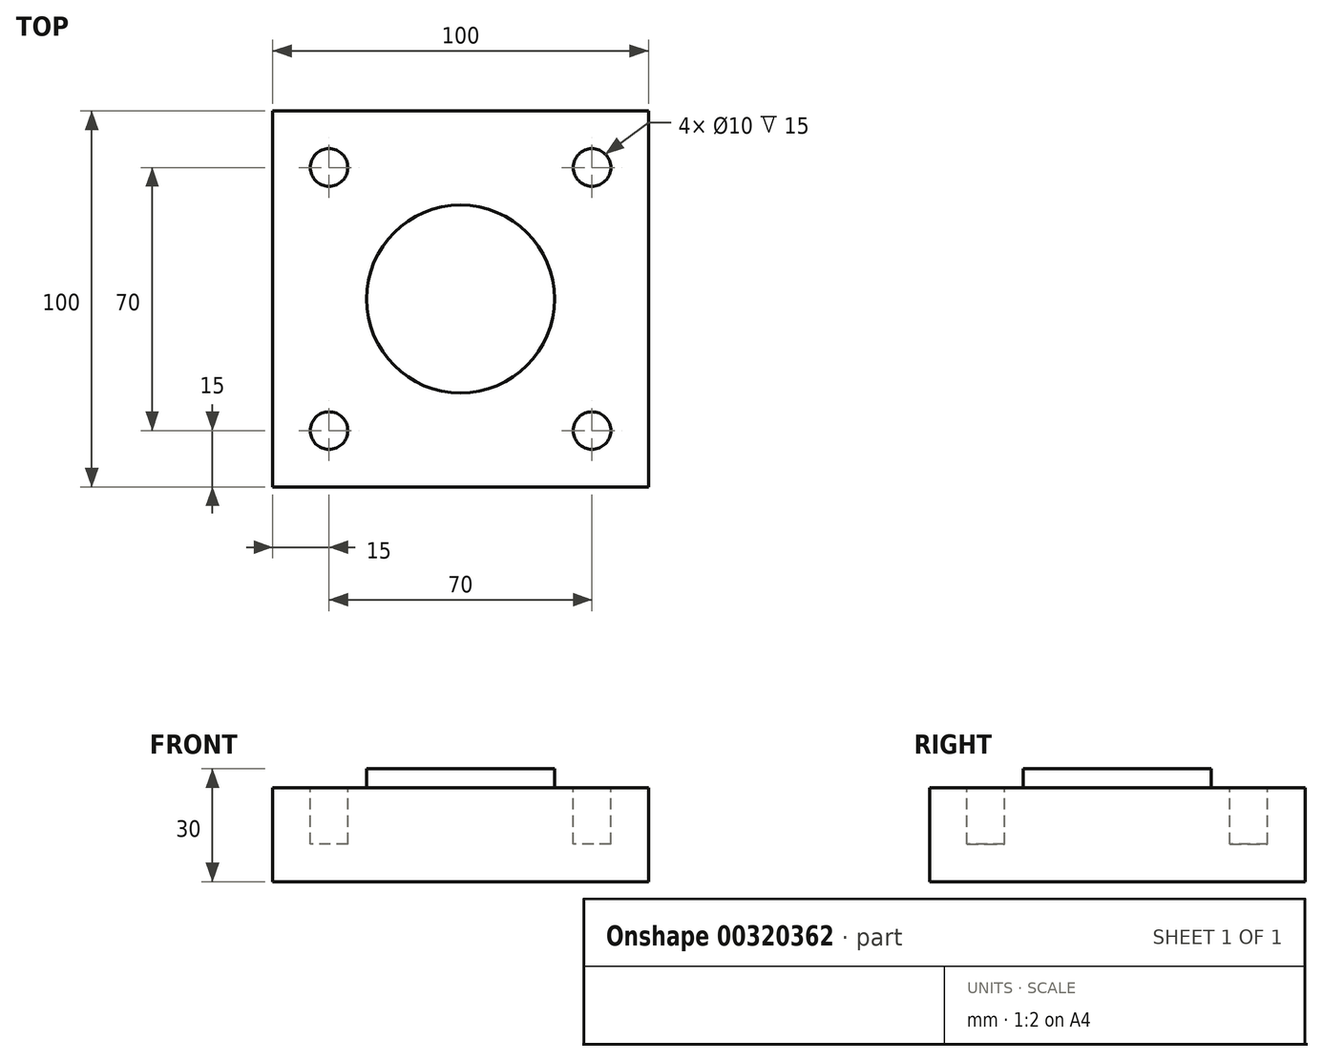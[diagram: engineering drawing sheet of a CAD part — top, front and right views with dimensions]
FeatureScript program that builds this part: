
annotation { "Feature Type Name" : "Feature", "Feature Type Description" : "" }
export const myFeature = defineFeature(function(context is Context, id is Id, definition is map)
    precondition{}
    {
        {
            var Q0;
            Q0=qCreatedBy(makeId("Top.planeOp"),FACE);
            var sketch = newSketch(context, id + "F0", { "sketchPlane" : qUnion([Q0])});
            skLineSegment(sketch, "E0.bottom", {"start": v(50, 50) * mm, "end": v(-50, 50) * mm});
            skLineSegment(sketch, "E0.top", {"start": v(50, -50) * mm, "end": v(-50, -50) * mm});
            skLineSegment(sketch, "E0.left", {"start": v(50, 50) * mm, "end": v(50, -50) * mm});
            skLineSegment(sketch, "E0.right", {"start": v(-50, 50) * mm, "end": v(-50, -50) * mm});
            skPoint(sketch, "E0.middle", {"position": v(0, 0) * mm});
            skSolve(sketch);
        }
        {
            var Q0;
            Q0=makeQuery(id+"F0.imprint","IMPRINT",FACE,{"disambiguationData":[TD([[makeQuery(id+"F0.imprint","IMPRINT",EDGE,{"derivedFrom":sQuery(id+"F0.wireOp",EDGE,"E0.bottom")}),1.0]])]});
            extrude(context, id + "F1", {"entities" : qUnion([Q0]), "depth" : 25 * mm});
        }
        {
            var Q0;
            Q0=makeQuery(id+"F1.opExtrude","CAP_FACE",FACE,{"disambiguationData":[OSD([sQuery(id+"F0.wireOp",EDGE,"E0.bottom"),sQuery(id+"F0.wireOp",EDGE,"E0.top"),sQuery(id+"F0.wireOp",EDGE,"E0.left"),sQuery(id+"F0.wireOp",EDGE,"E0.right")])],"isStart":false});
            var sketch = newSketch(context, id + "F2", { "sketchPlane" : qUnion([Q0])});
            skCircle(sketch, "E1", {"center": v(0, 0) * mm, "radius": 25 * mm});
            skSolve(sketch);
        }
        {
            var Q0;
            Q0=makeQuery(id+"F2.imprint","IMPRINT",FACE,{"disambiguationData":[TD([[makeQuery(id+"F2.imprint","IMPRINT",EDGE,{"derivedFrom":sQuery(id+"F2.wireOp",EDGE,"E1")}),1.0]])]});
            extrude(context, id + "F3", {"entities" : qUnion([Q0]), "operationType" : NewBodyOperationType.ADD, "depth" : 5 * mm});
        }
        {
            var Q0;
            Q0=makeQuery(id+"F1.opExtrude","CAP_FACE",FACE,{"disambiguationData":[OSD([sQuery(id+"F0.wireOp",EDGE,"E0.bottom"),sQuery(id+"F0.wireOp",EDGE,"E0.top"),sQuery(id+"F0.wireOp",EDGE,"E0.left"),sQuery(id+"F0.wireOp",EDGE,"E0.right")])],"isStart":false});
            var sketch = newSketch(context, id + "F4", { "sketchPlane" : qUnion([Q0])});
            skCircle(sketch, "E2", {"center": v(-35, 35) * mm, "radius": 5 * mm});
            skCircle(sketch, "E3", {"center": v(-35, -35) * mm, "radius": 5 * mm});
            skCircle(sketch, "E4", {"center": v(35, -35) * mm, "radius": 5 * mm});
            skCircle(sketch, "E5", {"center": v(35, 35) * mm, "radius": 5 * mm});
            skSolve(sketch);
        }
        {
            var Q0;
            Q0=makeQuery(id+"F4.imprint","IMPRINT",FACE,{"disambiguationData":[TD([[makeQuery(id+"F4.imprint","IMPRINT",EDGE,{"derivedFrom":sQuery(id+"F4.wireOp",EDGE,"E3")}),1.0]])]});
            var Q1;
            Q1=makeQuery(id+"F4.imprint","IMPRINT",FACE,{"disambiguationData":[TD([[makeQuery(id+"F4.imprint","IMPRINT",EDGE,{"derivedFrom":sQuery(id+"F4.wireOp",EDGE,"E2")}),1.0]])]});
            var Q2;
            Q2=makeQuery(id+"F4.imprint","IMPRINT",FACE,{"disambiguationData":[TD([[makeQuery(id+"F4.imprint","IMPRINT",EDGE,{"derivedFrom":sQuery(id+"F4.wireOp",EDGE,"E5")}),1.0]])]});
            var Q3;
            Q3=makeQuery(id+"F4.imprint","IMPRINT",FACE,{"disambiguationData":[TD([[makeQuery(id+"F4.imprint","IMPRINT",EDGE,{"derivedFrom":sQuery(id+"F4.wireOp",EDGE,"E4")}),1.0]])]});
            extrude(context, id + "F5", {"entities" : qUnion([Q0, Q1, Q2, Q3]), "operationType" : NewBodyOperationType.REMOVE, "oppositeDirection" : true, "depth" : 15 * mm});
        }
    });
